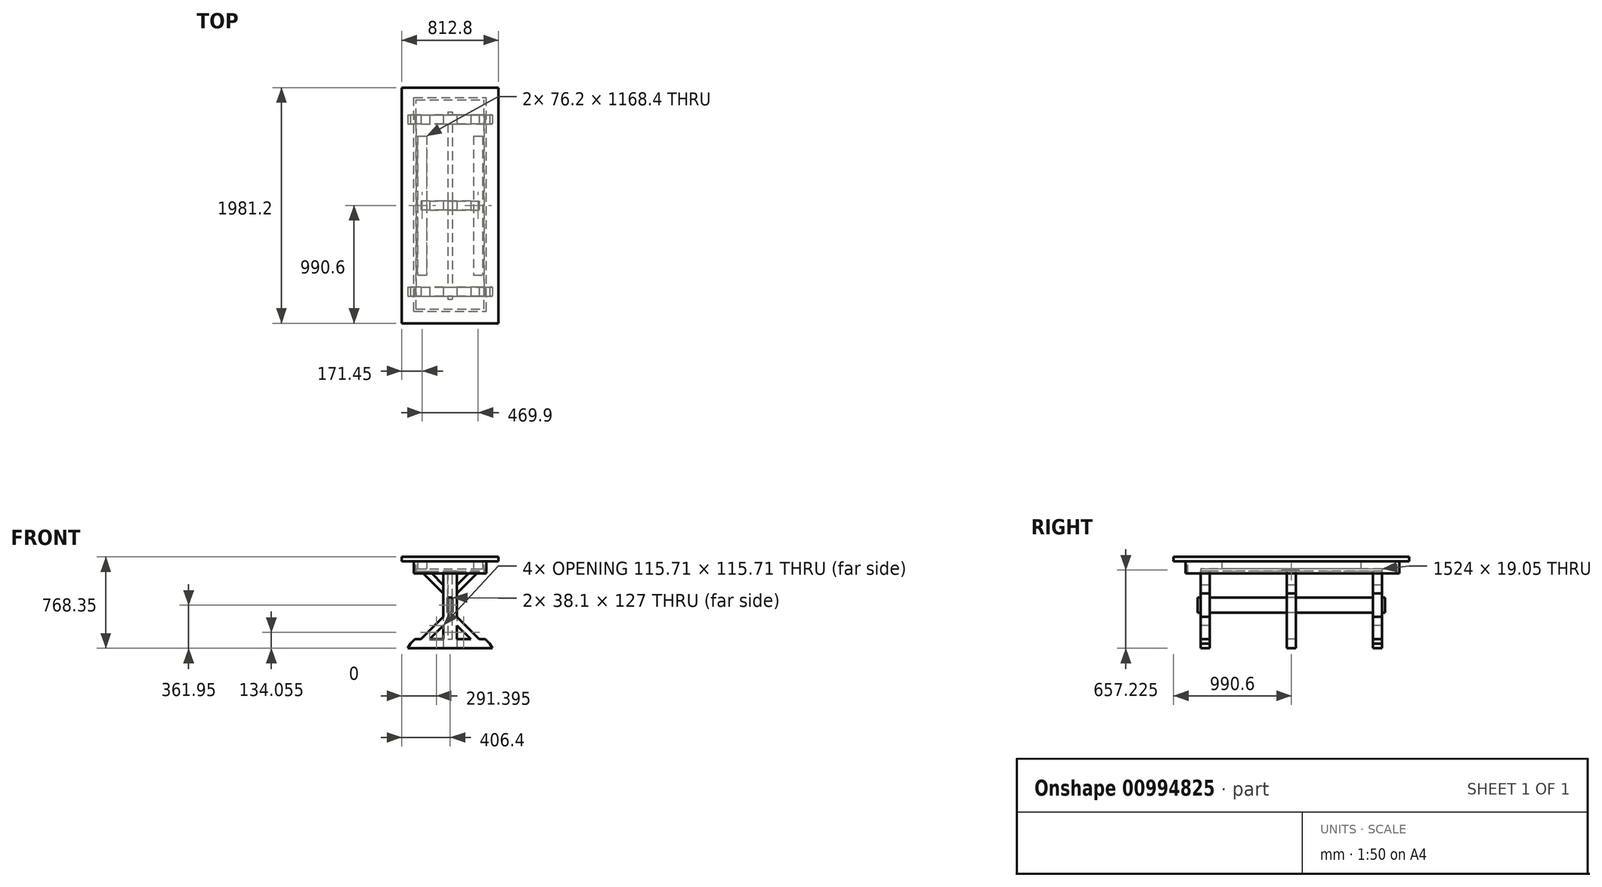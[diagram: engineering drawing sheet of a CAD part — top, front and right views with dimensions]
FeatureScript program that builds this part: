
annotation { "Feature Type Name" : "Feature", "Feature Type Description" : "" }
export const myFeature = defineFeature(function(context is Context, id is Id, definition is map)
    precondition{}
    {
        {
            var Q0;
            Q0=qCreatedBy(makeId("Front.planeOp"),FACE);
            var sketch = newSketch(context, id + "F0", { "sketchPlane" : qUnion([Q0])});
            skLineSegment(sketch, "E0", {"start": v(0, 76.2) * mm, "end": v(-295.5, 76.2) * mm});
            skLineSegment(sketch, "E1", {"start": v(-295.5, 76.2) * mm, "end": v(-333.6, 38.1) * mm});
            skLineSegment(sketch, "E2", {"start": v(0, 0) * mm, "end": v(0, 762) * mm, "construction": true});
            skLineSegment(sketch, "E3", {"start": v(-333.6, 38.1) * mm, "end": v(0, 38.1) * mm});
            skLineSegment(sketch, "E4", {"start": v(0, 76.2) * mm, "end": v(-19.05, 76.2) * mm});
            skLineSegment(sketch, "E5", {"start": v(-19.05, 76.2) * mm, "end": v(-19.05, 298.45) * mm});
            skLineSegment(sketch, "E6", {"start": v(-19.05, 298.45) * mm, "end": v(0, 298.45) * mm});
            skLineSegment(sketch, "E7", {"start": v(-19.05, 76.2) * mm, "end": v(-57.15, 76.2) * mm});
            skLineSegment(sketch, "E8", {"start": v(-57.15, 76.2) * mm, "end": v(-57.15, 647.7) * mm});
            skLineSegment(sketch, "E9", {"start": v(-57.15, 647.7) * mm, "end": v(-19.05, 647.7) * mm});
            skLineSegment(sketch, "E10", {"start": v(-19.05, 647.7) * mm, "end": v(-19.05, 76.2) * mm});
            skLineSegment(sketch, "E11", {"start": v(-355.6, 0) * mm, "end": v(0, 0) * mm});
            skLineSegment(sketch, "E12", {"start": v(0, 762) * mm, "end": v(-406.4, 762) * mm});
            skLineSegment(sketch, "E13", {"start": v(-406.4, 762) * mm, "end": v(-406.4, 723.9) * mm});
            skLineSegment(sketch, "E14", {"start": v(-406.4, 723.9) * mm, "end": v(0, 723.9) * mm});
            skLineSegment(sketch, "E15.bottom", {"start": v(-266.7, 723.9) * mm, "end": v(-200.03, 723.9) * mm, "construction": true});
            skLineSegment(sketch, "E15.top", {"start": v(-266.7, 666.75) * mm, "end": v(-200.03, 666.75) * mm, "construction": true});
            skLineSegment(sketch, "E15.left", {"start": v(-266.7, 723.9) * mm, "end": v(-266.7, 666.75) * mm, "construction": true});
            skLineSegment(sketch, "E15.right", {"start": v(-200.03, 723.9) * mm, "end": v(-200.03, 666.75) * mm, "construction": true});
            skLineSegment(sketch, "E16.bottom", {"start": v(-285.75, 666.75) * mm, "end": v(0, 666.75) * mm});
            skLineSegment(sketch, "E16.top", {"start": v(-285.75, 647.7) * mm, "end": v(0, 647.7) * mm});
            skLineSegment(sketch, "E16.left", {"start": v(-285.75, 666.75) * mm, "end": v(-285.75, 647.7) * mm});
            skLineSegment(sketch, "E17.bottom", {"start": v(-304.8, 723.9) * mm, "end": v(-285.75, 723.9) * mm});
            skLineSegment(sketch, "E17.top", {"start": v(-304.8, 622.3) * mm, "end": v(-285.75, 622.3) * mm});
            skLineSegment(sketch, "E17.left", {"start": v(-304.8, 723.9) * mm, "end": v(-304.8, 622.3) * mm});
            skLineSegment(sketch, "E17.right", {"start": v(-285.75, 723.9) * mm, "end": v(-285.75, 622.3) * mm});
            skLineSegment(sketch, "E18", {"start": v(-355.6, 0) * mm, "end": v(-333.6, 38.1) * mm});
            skLineSegment(sketch, "E19", {"start": v(-19.05, 647.7) * mm, "end": v(-19.05, 425.45) * mm});
            skLineSegment(sketch, "E20", {"start": v(-19.05, 425.45) * mm, "end": v(0, 425.45) * mm});
            skPoint(sketch, "E21", {"position": v(-19.05, 361.95) * mm});
            skLineSegment(sketch, "E22.MirrorCS", {"start": v(355.6, 0) * mm, "end": v(0, 0) * mm});
            skLineSegment(sketch, "E23.MirrorCS", {"start": v(333.6, 38.1) * mm, "end": v(0, 38.1) * mm});
            skLineSegment(sketch, "E24.MirrorCS", {"start": v(355.6, 0) * mm, "end": v(333.6, 38.1) * mm});
            skLineSegment(sketch, "E25.MirrorCS", {"start": v(295.5, 76.2) * mm, "end": v(333.6, 38.1) * mm});
            skLineSegment(sketch, "E26.MirrorCS", {"start": v(0, 76.2) * mm, "end": v(295.5, 76.2) * mm});
            skLineSegment(sketch, "E27.MirrorCS", {"start": v(57.15, 76.2) * mm, "end": v(57.15, 647.7) * mm});
            skLineSegment(sketch, "E28.MirrorCS", {"start": v(19.05, 647.7) * mm, "end": v(19.05, 76.2) * mm});
            skLineSegment(sketch, "E29.MirrorCS", {"start": v(19.05, 76.2) * mm, "end": v(57.15, 76.2) * mm});
            skLineSegment(sketch, "E30.MirrorCS", {"start": v(0, 762) * mm, "end": v(406.4, 762) * mm});
            skLineSegment(sketch, "E31.MirrorCS", {"start": v(406.4, 762) * mm, "end": v(406.4, 723.9) * mm});
            skLineSegment(sketch, "E32.MirrorCS", {"start": v(406.4, 723.9) * mm, "end": v(0, 723.9) * mm});
            skLineSegment(sketch, "E33.MirrorCS", {"start": v(285.75, 723.9) * mm, "end": v(285.75, 622.3) * mm});
            skLineSegment(sketch, "E34.MirrorCS", {"start": v(304.8, 723.9) * mm, "end": v(304.8, 622.3) * mm});
            skLineSegment(sketch, "E35.MirrorCS", {"start": v(304.8, 622.3) * mm, "end": v(285.75, 622.3) * mm});
            skLineSegment(sketch, "E36.MirrorCS", {"start": v(285.75, 647.7) * mm, "end": v(0, 647.7) * mm});
            skLineSegment(sketch, "E37.MirrorCS", {"start": v(266.7, 666.75) * mm, "end": v(200.03, 666.75) * mm, "construction": true});
            skLineSegment(sketch, "E38.MirrorCS", {"start": v(266.7, 723.9) * mm, "end": v(266.7, 666.75) * mm, "construction": true});
            skLineSegment(sketch, "E39.MirrorCS", {"start": v(200.03, 723.9) * mm, "end": v(200.03, 666.75) * mm, "construction": true});
            skLineSegment(sketch, "E40.MirrorCS", {"start": v(266.7, 723.9) * mm, "end": v(200.03, 723.9) * mm, "construction": true});
            skLineSegment(sketch, "E41.MirrorCS", {"start": v(285.75, 666.75) * mm, "end": v(0, 666.75) * mm});
            skLineSegment(sketch, "E42.MirrorCS", {"start": v(19.05, 425.45) * mm, "end": v(0, 425.45) * mm});
            skLineSegment(sketch, "E43.MirrorCS", {"start": v(19.05, 298.45) * mm, "end": v(0, 298.45) * mm});
            skLineSegment(sketch, "E44", {"start": v(57.15, 191.91) * mm, "end": v(172.86, 76.2) * mm});
            skLineSegment(sketch, "E45", {"start": v(172.86, 76.2) * mm, "end": v(244.7, 76.2) * mm});
            skLineSegment(sketch, "E46", {"start": v(244.7, 76.2) * mm, "end": v(57.15, 263.75) * mm});
            skLineSegment(sketch, "E47", {"start": v(57.15, 263.75) * mm, "end": v(57.15, 191.91) * mm});
            skLineSegment(sketch, "E48", {"start": v(-19.05, 361.95) * mm, "end": v(417.93, 361.95) * mm, "construction": true});
            skLineSegment(sketch, "E49.MirrorCS", {"start": v(244.7, 647.7) * mm, "end": v(57.15, 460.15) * mm});
            skLineSegment(sketch, "E50.MirrorCS", {"start": v(57.15, 531.99) * mm, "end": v(172.86, 647.7) * mm});
            skLineSegment(sketch, "E51.MirrorCS", {"start": v(-244.7, 76.2) * mm, "end": v(-57.15, 263.75) * mm});
            skLineSegment(sketch, "E52.MirrorCS", {"start": v(-57.15, 191.91) * mm, "end": v(-172.86, 76.2) * mm});
            skLineSegment(sketch, "E53.MirrorCS", {"start": v(-244.7, 647.7) * mm, "end": v(-57.15, 460.15) * mm});
            skLineSegment(sketch, "E54.MirrorCS", {"start": v(-57.15, 531.99) * mm, "end": v(-172.86, 647.7) * mm});
            skSolve(sketch);
        }
        {
            var Q0;
            Q0=makeQuery(id+"F0.imprint","IMPRINT",FACE,{"disambiguationData":[TD([[makeQuery(id+"F0.imprint","IMPRINT",EDGE,{"derivedFrom":sQuery(id+"F0.wireOp",EDGE,"E3")}),-1.0]])]});
            var Q1;
            {var subQ4=sQuery(id+"F0.wireOp",EDGE,"E1");Q1=makeQuery(id+"F0.imprint","IMPRINT",FACE,{"disambiguationData":[TD([[makeQuery(id+"F0.imprint","IMPRINT",EDGE,{"derivedFrom":subQ4}),1.0]])]});}
            extrude(context, id + "F1", {"entities" : qUnion([Q0, Q1]), "oppositeDirection" : true, "depth" : 76.2 * mm, "offsetDistance" : 25.4 * mm});
        }
        {
            var Q0;
            {var subQ0=sQuery(id+"F0.wireOp",EDGE,"E27.MirrorCS");var subQ4=sQuery(id+"F0.wireOp",EDGE,"E26.MirrorCS");var subQ5=makeQuery(id+"F0.imprint","INTERSECT",VERTEX,{"derivedFrom":[subQ4,subQ0]});Q0=makeQuery(id+"F0.imprint","IMPRINT",FACE,{"disambiguationData":[TD([[makeQuery(id+"F0.imprint","IMPRINT",EDGE,{"disambiguationData":[TD([[subQ5,1.0]])],"derivedFrom":subQ4}),1.0]])]});}
            var Q1;
            {var subQ6=sQuery(id+"F0.wireOp",EDGE,"E5");Q1=makeQuery(id+"F0.imprint","IMPRINT",FACE,{"disambiguationData":[TD([[makeQuery(id+"F0.imprint","IMPRINT",EDGE,{"derivedFrom":subQ6}),1.0]])]});}
            extrude(context, id + "F2", {"entities" : qUnion([Q0, Q1]), "operationType" : NewBodyOperationType.ADD, "oppositeDirection" : true, "depth" : 76.2 * mm, "offsetDistance" : 25.4 * mm});
        }
        {
            var Q0;
            {var subQ0=sQuery(id+"F0.wireOp",EDGE,"E51.MirrorCS");Q0=makeQuery(id+"F0.imprint","IMPRINT",FACE,{"disambiguationData":[TD([[makeQuery(id+"F0.imprint","IMPRINT",EDGE,{"derivedFrom":subQ0}),-1.0]])]});}
            var Q1;
            {var subQ0=sQuery(id+"F0.wireOp",EDGE,"E44");Q1=makeQuery(id+"F0.imprint","IMPRINT",FACE,{"disambiguationData":[TD([[makeQuery(id+"F0.imprint","IMPRINT",EDGE,{"derivedFrom":subQ0}),1.0]])]});}
            extrude(context, id + "F3", {"entities" : qUnion([Q0, Q1]), "operationType" : NewBodyOperationType.ADD, "oppositeDirection" : true, "depth" : 76.2 * mm, "offsetDistance" : 25.4 * mm});
        }
        {
            var Q0;
            {var subQ5=sQuery(id+"F0.wireOp",EDGE,"E5");Q0=makeQuery(id+"F0.imprint","IMPRINT",FACE,{"disambiguationData":[TD([[makeQuery(id+"F0.imprint","IMPRINT",EDGE,{"derivedFrom":subQ5}),-1.0]])]});}
            var Q1;
            {var subQ0=sQuery(id+"F0.wireOp",EDGE,"E20");Q1=makeQuery(id+"F0.imprint","IMPRINT",FACE,{"disambiguationData":[TD([[makeQuery(id+"F0.imprint","IMPRINT",EDGE,{"derivedFrom":subQ0}),1.0]])]});}
            extrude(context, id + "F4", {"entities" : qUnion([Q0, Q1]), "oppositeDirection" : true, "depth" : 76.2 * mm, "offsetDistance" : 25.4 * mm});
        }
        {
            var Q0;
            {var subQ2=sQuery(id+"F0.wireOp",EDGE,"E53.MirrorCS");Q0=makeQuery(id+"F0.imprint","IMPRINT",FACE,{"disambiguationData":[TD([[makeQuery(id+"F0.imprint","IMPRINT",EDGE,{"derivedFrom":subQ2}),1.0]])]});}
            var Q1;
            {var subQ2=sQuery(id+"F0.wireOp",EDGE,"E49.MirrorCS");Q1=makeQuery(id+"F0.imprint","IMPRINT",FACE,{"disambiguationData":[TD([[makeQuery(id+"F0.imprint","IMPRINT",EDGE,{"derivedFrom":subQ2}),-1.0]])]});}
            extrude(context, id + "F5", {"entities" : qUnion([Q0, Q1]), "oppositeDirection" : true, "depth" : 76.2 * mm, "offsetDistance" : 25.4 * mm});
        }
        {
            var Q0;
            {var subQ0=sQuery(id+"F0.wireOp",EDGE,"E27.MirrorCS");var subQ1=sQuery(id+"F0.wireOp",EDGE,"E26.MirrorCS");var subQ2=sQuery(id+"F0.wireOp",EDGE,"E8");var subQ3=sQuery(id+"F0.wireOp",EDGE,"E0");Q0=makeQuery(id+"F3.boolean.opBoolean","MERGE",FACE,{"derivedFrom":[makeQuery(id+"F2.boolean.opBoolean","MERGE",FACE,{"derivedFrom":[makeQuery(id+"F1.opExtrude","CAP_FACE",FACE,{"disambiguationData":[OSD([subQ3,sQuery(id+"F0.wireOp",EDGE,"E1"),sQuery(id+"F0.wireOp",EDGE,"E11"),sQuery(id+"F0.wireOp",EDGE,"E18"),sQuery(id+"F0.wireOp",EDGE,"E22.MirrorCS"),sQuery(id+"F0.wireOp",EDGE,"E24.MirrorCS"),sQuery(id+"F0.wireOp",EDGE,"E25.MirrorCS"),subQ1])],"isStart":false}),makeQuery(id+"F2.opExtrude","CAP_FACE",FACE,{"disambiguationData":[OSD([subQ3,sQuery(id+"F0.wireOp",EDGE,"E5"),subQ2,sQuery(id+"F0.wireOp",EDGE,"E9"),sQuery(id+"F0.wireOp",EDGE,"E10")])],"isStart":false}),makeQuery(id+"F2.opExtrude","CAP_FACE",FACE,{"disambiguationData":[OSD([subQ1,subQ0,sQuery(id+"F0.wireOp",EDGE,"E28.MirrorCS"),sQuery(id+"F0.wireOp",EDGE,"E36.MirrorCS")])],"isStart":false})]}),makeQuery(id+"F3.opExtrude","CAP_FACE",FACE,{"disambiguationData":[OSD([subQ3,subQ2,sQuery(id+"F0.wireOp",EDGE,"E51.MirrorCS"),sQuery(id+"F0.wireOp",EDGE,"E52.MirrorCS")])],"isStart":false}),makeQuery(id+"F3.opExtrude","CAP_FACE",FACE,{"disambiguationData":[OSD([subQ1,subQ0,sQuery(id+"F0.wireOp",EDGE,"E44"),sQuery(id+"F0.wireOp",EDGE,"E46")])],"isStart":false})]});}
            var Q1;
            Q1=makeQuery(id+"F5.opExtrude","CAP_FACE",FACE,{"disambiguationData":[OSD([sQuery(id+"F0.wireOp",EDGE,"E27.MirrorCS"),sQuery(id+"F0.wireOp",EDGE,"E36.MirrorCS"),sQuery(id+"F0.wireOp",EDGE,"E49.MirrorCS"),sQuery(id+"F0.wireOp",EDGE,"E50.MirrorCS")])],"isStart":false});
            var Q2;
            Q2=makeQuery(id+"F5.opExtrude","CAP_FACE",FACE,{"disambiguationData":[OSD([sQuery(id+"F0.wireOp",EDGE,"E8"),sQuery(id+"F0.wireOp",EDGE,"E16.top"),sQuery(id+"F0.wireOp",EDGE,"E53.MirrorCS"),sQuery(id+"F0.wireOp",EDGE,"E54.MirrorCS")])],"isStart":false});
            var Q3;
            Q3=makeQuery(id+"F4.opExtrude","CAP_FACE",FACE,{"disambiguationData":[OSD([sQuery(id+"F0.wireOp",EDGE,"E10"),sQuery(id+"F0.wireOp",EDGE,"E16.top"),sQuery(id+"F0.wireOp",EDGE,"E20"),sQuery(id+"F0.wireOp",EDGE,"E28.MirrorCS"),sQuery(id+"F0.wireOp",EDGE,"E36.MirrorCS"),sQuery(id+"F0.wireOp",EDGE,"E42.MirrorCS")])],"isStart":false});
            var Q4;
            Q4=makeQuery(id+"F4.opExtrude","CAP_FACE",FACE,{"disambiguationData":[OSD([sQuery(id+"F0.wireOp",EDGE,"E0"),sQuery(id+"F0.wireOp",EDGE,"E5"),sQuery(id+"F0.wireOp",EDGE,"E6"),sQuery(id+"F0.wireOp",EDGE,"E26.MirrorCS"),sQuery(id+"F0.wireOp",EDGE,"E28.MirrorCS"),sQuery(id+"F0.wireOp",EDGE,"E43.MirrorCS")])],"isStart":false});
            extrude(context, id + "F6", {"entities" : qUnion([Q0, Q1, Q2, Q3, Q4]), "depth" : 1447.8 * mm, "offsetDistance" : 25.4 * mm});
        }
        {
            var Q0;
            Q0=qCreatedBy(makeId("Right.planeOp"),FACE);
            var sketch = newSketch(context, id + "F7", { "sketchPlane" : qUnion([Q0])});
            skLineSegment(sketch, "E55.bottom", {"start": v(76.2, -1.7) * mm, "end": v(723.9, -1.7) * mm});
            skLineSegment(sketch, "E55.top", {"start": v(76.2, 696.31) * mm, "end": v(723.9, 696.31) * mm});
            skLineSegment(sketch, "E55.left", {"start": v(76.2, -1.7) * mm, "end": v(76.2, 696.31) * mm});
            skLineSegment(sketch, "E55.right", {"start": v(1447.8, -1.7) * mm, "end": v(1447.8, 696.31) * mm});
            skLineSegment(sketch, "E56.left", {"start": v(800.1, 696.31) * mm, "end": v(800.1, -1.7) * mm});
            skLineSegment(sketch, "E56.right", {"start": v(723.9, 696.31) * mm, "end": v(723.9, -1.7) * mm});
            skPoint(sketch, "E57", {"position": v(762, 696.31) * mm});
            skLineSegment(sketch, "E58.trimOffspring", {"start": v(800.1, -1.7) * mm, "end": v(1447.8, -1.7) * mm});
            skLineSegment(sketch, "E59.trimOffspring", {"start": v(800.1, 696.31) * mm, "end": v(1447.8, 696.31) * mm});
            skSolve(sketch);
        }
        {
            var Q0;
            Q0 = qSketchRegion(id + "F7", true);
            extrude(context, id + "F8", {"entities" : qUnion([Q0]), "operationType" : NewBodyOperationType.REMOVE, "endBound" : BoundingType.SYMMETRIC, "oppositeDirection" : true, "depth" : 1016 * mm, "offsetDistance" : 25.4 * mm});
        }
        {
            var Q0;
            {var subQ5=sQuery(id+"F0.wireOp",EDGE,"E6");Q0=makeQuery(id+"F0.imprint","IMPRINT",FACE,{"disambiguationData":[TD([[makeQuery(id+"F0.imprint","IMPRINT",EDGE,{"derivedFrom":subQ5}),1.0]])]});}
            extrude(context, id + "F9", {"entities" : qUnion([Q0]), "oppositeDirection" : true, "depth" : 1524 * mm, "offsetDistance" : 25.4 * mm});
        }
        {
            var Q0;
            {var subQ5=sQuery(id+"F0.wireOp",EDGE,"E6");Q0=makeQuery(id+"F0.imprint","IMPRINT",FACE,{"disambiguationData":[TD([[makeQuery(id+"F0.imprint","IMPRINT",EDGE,{"derivedFrom":subQ5}),1.0]])]});}
            extrude(context, id + "F10", {"entities" : qUnion([Q0]), "operationType" : NewBodyOperationType.ADD, "depth" : 25.4 * mm, "offsetDistance" : 25.4 * mm});
        }
        {
            var Q0;
            Q0=makeQuery(id+"F9.opExtrude","CAP_FACE",FACE,{"disambiguationData":[OSD([sQuery(id+"F0.wireOp",EDGE,"E6"),sQuery(id+"F0.wireOp",EDGE,"E10"),sQuery(id+"F0.wireOp",EDGE,"E20"),sQuery(id+"F0.wireOp",EDGE,"E28.MirrorCS"),sQuery(id+"F0.wireOp",EDGE,"E42.MirrorCS"),sQuery(id+"F0.wireOp",EDGE,"E43.MirrorCS")])],"isStart":false});
            extrude(context, id + "F11", {"entities" : qUnion([Q0]), "operationType" : NewBodyOperationType.ADD, "depth" : 25.4 * mm, "offsetDistance" : 25.4 * mm});
        }
        {
            var Q0;
            {var subQ4=sQuery(id+"F0.wireOp",EDGE,"E36.MirrorCS");var subQ5=makeQuery(id+"F6.opExtrude","SWEPT_FACE",FACE,{"disambiguationData":[OSD([subQ4]),TDD([makeQuery(id+"F5.opExtrude","CAP_EDGE",EDGE,{"disambiguationData":[OSD([subQ4])],"isStart":false})])]});Q0=qUnion([makeQuery(id+"F8.boolean.opBoolean","SPLIT",FACE,{"disambiguationData":[TD([makeQuery(id+"F8.opExtrude","SWEPT_FACE",FACE,{"disambiguationData":[OSD([sQuery(id+"F7.wireOp",EDGE,"E55.right")])]})])],"derivedFrom":subQ5}),makeQuery(id+"F8.boolean.opBoolean","SPLIT",FACE,{"disambiguationData":[TD([makeQuery(id+"F8.opExtrude","SWEPT_FACE",FACE,{"disambiguationData":[OSD([sQuery(id+"F7.wireOp",EDGE,"E56.left")])]})])],"derivedFrom":subQ5})]);}
            var sketch = newSketch(context, id + "F12", { "sketchPlane" : qUnion([Q0])});
            skLineSegment(sketch, "E60.bottom", {"start": v(-285.75, 1524) * mm, "end": v(285.75, 1524) * mm});
            skLineSegment(sketch, "E60.top", {"start": v(-285.75, 0) * mm, "end": v(285.75, 0) * mm});
            skLineSegment(sketch, "E60.left", {"start": v(-285.75, 1524) * mm, "end": v(-285.75, 0) * mm});
            skLineSegment(sketch, "E60.right", {"start": v(285.75, 1524) * mm, "end": v(285.75, 0) * mm});
            skSolve(sketch);
        }
        {
            var Q0;
            Q0 = qSketchRegion(id + "F12", true);
            extrude(context, id + "F13", {"entities" : qUnion([Q0]), "depth" : 19.05 * mm, "offsetDistance" : 25.4 * mm});
        }
        {
            var Q0;
            Q0=makeQuery(id+"F13.opExtrude","CAP_FACE",FACE,{"disambiguationData":[OSD([sQuery(id+"F12.wireOp",EDGE,"E60.bottom"),sQuery(id+"F12.wireOp",EDGE,"E60.top"),sQuery(id+"F12.wireOp",EDGE,"E60.left"),sQuery(id+"F12.wireOp",EDGE,"E60.right")])],"isStart":false});
            var sketch = newSketch(context, id + "F14", { "sketchPlane" : qUnion([Q0])});
            skLineSegment(sketch, "E61", {"start": v(-273.05, 762) * mm, "end": v(273.05, 762) * mm, "construction": true});
            skLineSegment(sketch, "E62.bottom", {"start": v(-273.05, 1346.2) * mm, "end": v(-196.85, 1346.2) * mm});
            skLineSegment(sketch, "E62.top", {"start": v(-273.05, 177.8) * mm, "end": v(-196.85, 177.8) * mm});
            skLineSegment(sketch, "E62.left", {"start": v(-273.05, 1346.2) * mm, "end": v(-273.05, 177.8) * mm});
            skLineSegment(sketch, "E62.right", {"start": v(-196.85, 1346.2) * mm, "end": v(-196.85, 177.8) * mm});
            skLineSegment(sketch, "E63.bottom", {"start": v(196.85, 1346.2) * mm, "end": v(273.05, 1346.2) * mm});
            skLineSegment(sketch, "E63.top", {"start": v(196.85, 177.8) * mm, "end": v(273.05, 177.8) * mm});
            skLineSegment(sketch, "E63.left", {"start": v(196.85, 1346.2) * mm, "end": v(196.85, 177.8) * mm});
            skLineSegment(sketch, "E63.right", {"start": v(273.05, 1346.2) * mm, "end": v(273.05, 177.8) * mm});
            skSolve(sketch);
        }
        {
            var Q0;
            Q0=makeQuery(id+"F14.imprint","IMPRINT",FACE,{"disambiguationData":[TD([[makeQuery(id+"F14.imprint","IMPRINT",EDGE,{"derivedFrom":sQuery(id+"F14.wireOp",EDGE,"E62.bottom")}),-1.0]])]});
            var Q1;
            Q1=makeQuery(id+"F14.imprint","IMPRINT",FACE,{"disambiguationData":[TD([[makeQuery(id+"F14.imprint","IMPRINT",EDGE,{"derivedFrom":sQuery(id+"F14.wireOp",EDGE,"E63.bottom")}),-1.0]])]});
            extrude(context, id + "F15", {"entities" : qUnion([Q0, Q1]), "operationType" : NewBodyOperationType.ADD, "depth" : 63.5 * mm, "offsetDistance" : 25.4 * mm});
        }
        {
            var Q0;
            Q0=makeQuery(id+"F15.opExtrude","CAP_FACE",FACE,{"disambiguationData":[OSD([sQuery(id+"F14.wireOp",EDGE,"E62.bottom"),sQuery(id+"F14.wireOp",EDGE,"E62.top"),sQuery(id+"F14.wireOp",EDGE,"E62.left"),sQuery(id+"F14.wireOp",EDGE,"E62.right")])],"isStart":false});
            var sketch = newSketch(context, id + "F16", { "sketchPlane" : qUnion([Q0])});
            skLineSegment(sketch, "E64.bottom", {"start": v(-406.4, 1752.6) * mm, "end": v(406.4, 1752.6) * mm});
            skLineSegment(sketch, "E64.top", {"start": v(-406.4, -228.6) * mm, "end": v(406.4, -228.6) * mm});
            skLineSegment(sketch, "E64.left", {"start": v(-406.4, 1752.6) * mm, "end": v(-406.4, -228.6) * mm});
            skLineSegment(sketch, "E64.right", {"start": v(406.4, 1752.6) * mm, "end": v(406.4, -228.6) * mm});
            skLineSegment(sketch, "E65", {"start": v(0, 0) * mm, "end": v(0, -228.6) * mm, "construction": true});
            skSolve(sketch);
        }
        {
            var Q0;
            Q0 = qSketchRegion(id + "F16", true);
            extrude(context, id + "F17", {"entities" : qUnion([Q0]), "operationType" : NewBodyOperationType.ADD, "depth" : 38.1 * mm, "offsetDistance" : 25.4 * mm});
        }
        {
            var Q0;
            Q0=makeQuery(id+"F17.opExtrude","CAP_FACE",FACE,{"disambiguationData":[OSD([sQuery(id+"F16.wireOp",EDGE,"E64.bottom"),sQuery(id+"F16.wireOp",EDGE,"E64.top"),sQuery(id+"F16.wireOp",EDGE,"E64.left"),sQuery(id+"F16.wireOp",EDGE,"E64.right")])],"isStart":true});
            var sketch = newSketch(context, id + "F18", { "sketchPlane" : qUnion([Q0])});
            skLineSegment(sketch, "E66.bottom", {"start": v(-304.8, 127) * mm, "end": v(304.8, 127) * mm});
            skLineSegment(sketch, "E66.top", {"start": v(-304.8, -1669.97) * mm, "end": v(304.8, -1669.97) * mm});
            skLineSegment(sketch, "E66.left", {"start": v(-304.8, 127) * mm, "end": v(-304.8, -1669.97) * mm});
            skLineSegment(sketch, "E66.right", {"start": v(304.8, 127) * mm, "end": v(304.8, -1669.97) * mm});
            skLineSegment(sketch, "E67.bottom", {"start": v(-285.75, 107.95) * mm, "end": v(285.75, 107.95) * mm});
            skLineSegment(sketch, "E67.top", {"start": v(-285.75, -1650.92) * mm, "end": v(273.05, -1650.92) * mm});
            skLineSegment(sketch, "E67.left", {"start": v(-285.75, 107.95) * mm, "end": v(-285.75, -1650.92) * mm});
            skLineSegment(sketch, "E67.right", {"start": v(285.75, 107.95) * mm, "end": v(285.75, -1650.92) * mm});
            skLineSegment(sketch, "E68", {"start": v(273.05, -1650.92) * mm, "end": v(285.75, -1650.92) * mm});
            skSolve(sketch);
        }
        {
            var Q0;
            Q0=makeQuery(id+"F18.imprint","IMPRINT",FACE,{"disambiguationData":[TD([[makeQuery(id+"F18.imprint","IMPRINT",EDGE,{"derivedFrom":sQuery(id+"F18.wireOp",EDGE,"E66.bottom")}),-1.0]])]});
            extrude(context, id + "F19", {"entities" : qUnion([Q0]), "operationType" : NewBodyOperationType.ADD, "depth" : 101.6 * mm, "offsetDistance" : 25.4 * mm});
        }
        {
            var Q0;
            {var subQ13=sQuery(id+"F0.wireOp",EDGE,"E1");Q0=makeQuery(id+"F8.boolean.opBoolean","COPY",FACE,{"disambiguationData":[TD([makeQuery(id+"F6.opExtrude","SWEPT_FACE",FACE,{"disambiguationData":[OSD([subQ13])]})])],"derivedFrom":makeQuery(id+"F8.opExtrude","SWEPT_FACE",FACE,{"disambiguationData":[OSD([sQuery(id+"F7.wireOp",EDGE,"E56.left")])]})});}
            var sketch = newSketch(context, id + "F20", { "sketchPlane" : qUnion([Q0])});
            skLineSegment(sketch, "E69.bottom", {"start": v(57.15, 263.75) * mm, "end": v(510, 263.75) * mm});
            skLineSegment(sketch, "E69.top", {"start": v(57.15, -83.18) * mm, "end": v(510, -83.18) * mm});
            skLineSegment(sketch, "E69.left", {"start": v(57.15, 263.75) * mm, "end": v(57.15, -83.18) * mm});
            skLineSegment(sketch, "E69.right", {"start": v(510, 263.75) * mm, "end": v(510, -83.18) * mm});
            skLineSegment(sketch, "E70.bottom", {"start": v(-57.15, 263.75) * mm, "end": v(-399.16, 263.75) * mm});
            skLineSegment(sketch, "E70.top", {"start": v(-57.15, -37.53) * mm, "end": v(-399.16, -37.53) * mm});
            skLineSegment(sketch, "E70.left", {"start": v(-57.15, 263.75) * mm, "end": v(-57.15, -37.53) * mm});
            skLineSegment(sketch, "E70.right", {"start": v(-399.16, 263.75) * mm, "end": v(-399.16, -37.53) * mm});
            skSolve(sketch);
        }
        {
            var Q0;
            Q0 = qSketchRegion(id + "F20", true);
            extrude(context, id + "F21", {"entities" : qUnion([Q0]), "operationType" : NewBodyOperationType.REMOVE, "oppositeDirection" : true, "depth" : 101.6 * mm, "offsetDistance" : 25.4 * mm});
        }
    });
